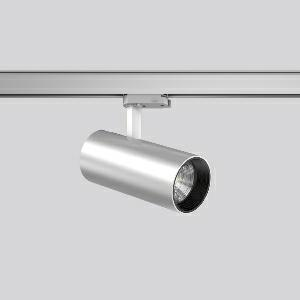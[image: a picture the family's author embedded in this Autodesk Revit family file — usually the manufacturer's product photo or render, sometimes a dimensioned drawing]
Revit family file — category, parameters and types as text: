
# Revit family: deecos_s_mini_742209_004_3_76_5d4f
name_source: partatom
category: Lighting Fixtures
units: mm (PartAtom-declared; Revit-internal decimal feet)

## family parameters
Cut with Voids When Loaded = No
Host = Face
Light Source = No
Part Type = Normal
Room Calculation Point = No
Round Connector Dimension = Use Diameter
Shared = No

## types (1)
- DEECOS S mini (1 x LED Modul 935, 3300 lm, 3500)
    Apparent Load = 29 VA
    Approval mark = CE
    CIE Flux Codes = 80 99 100 100 100
    Color Rendering = 92
    Color Temperature = 3500
    Default Elevation = 1800 mm
    Description = Series: DEECOS S mini
LED surface-mounted projector in modern design with no visible cooling ribs. Housing: die-cast aluminium, powder-coated. Rotation range: 356°. Swivel range: 90°. Black plastic ring and recessed LED to prevent glare from the side. Optical assembly with lens made of plastic (polycarbonate) for the best homogeneous light distribution - can be changed without tools. Best colour rendering index Ra>90. With adapter for RZB 3-circuit DALI tracks. Suitable for Track on ceiling, Wall track. High quality converter without flickering and stroboscopic effect. The following accessories can be mounted without use of tools: interchangeable lenses, decorative glasses, honeycomb louvre, clear and frosted diffusers, white interchangeable plastic ring. 
Colour: silver
Diameter: 87 mm
Height: 214 mm
Lamp: LED
Socket: without socket
Colour temperature: 3500K
Colour rendering index (CRI): 92
System power: 29 W
Rated luminous flux: 3300 lm
Luminous efficiency: 114 lm/W
Control gear: Converter, dimmable, DALI
Protection class: I
Type of protection: IP 20
    Height = 214 mm
    Lamp = 1 x LED Modul 935
    Lamp Light Flux = 3300 lm
    Lamp count = 1
    Length = 87 mm
    Lifetime = 50000 h
    Luminous efficacy = 114 lm/W
    Manufacturer = RZB
    ModVariant = No
    Model = 742209.004.3.76
    Mounting Place = Ceiling
    Mounting Type = Rail mounted
    Number of Poles = 1
    OnlyDefault = Yes
    Power Factor = 1
    Product Name = DEECOS S mini
    Product group = Track mounted projectors
    ProductGroupID = 301
    Protection Class = Protection class I
    Protection Degree = IP 20
    RLX_Detail_Level = 1
    RLX_Emergency_Light_Flux = 0 lm
    RLX_Emergency_Type = 0
    RLX_Emergency_Type_DB = No
    RlxData = <blob elided: 37237 chars, md5=8df1fe44>
    Socket = socket
    Standby Power = 0 W
    System Light Flux = 3300 lm
    System Power = 29 W
    Type Comments = Product without accessories
    Type Image = 741930.004.jpg
    URL = http://relux.com
    VarID = ---
    Voltage = 230 V
    Voltage Range = 220-240 V
    Weight = 0.00 kg
    Width = 0 mm  [stored 0 ft]

note: [stored X ft] marks values corroborated as IEEE doubles in the binary element streams (Revit-internal decimal feet)

## geometry (parser evidence)
native form markers: Blend x4, Sweep x12
no freeform markers — native parametric forms only
